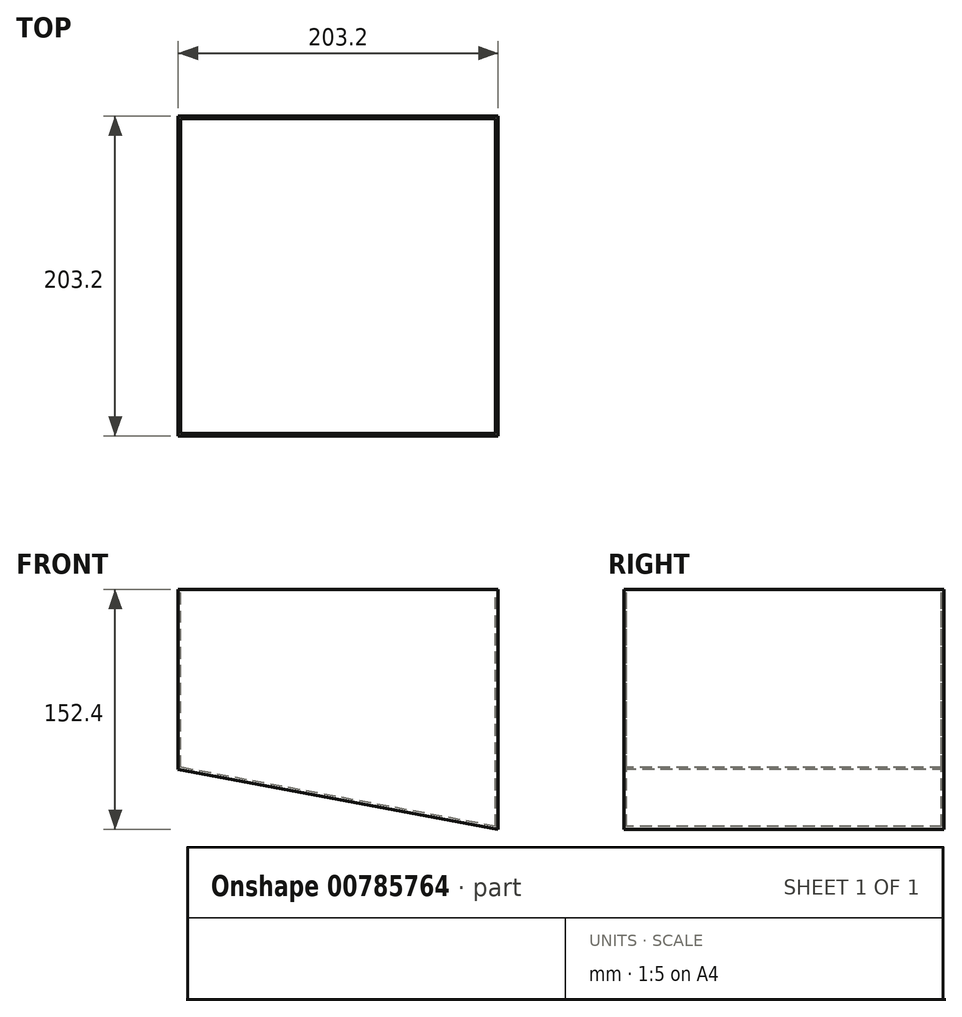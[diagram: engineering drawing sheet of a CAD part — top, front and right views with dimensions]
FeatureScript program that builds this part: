
annotation { "Feature Type Name" : "Feature", "Feature Type Description" : "" }
export const myFeature = defineFeature(function(context is Context, id is Id, definition is map)
    precondition{}
    {
        {
            var Q0;
            Q0=qCreatedBy(makeId("Front.planeOp"),FACE);
            var sketch = newSketch(context, id + "F0", { "sketchPlane" : qUnion([Q0])});
            skLineSegment(sketch, "E0.top", {"start": v(101.6, 76.2) * mm, "end": v(-101.6, 76.2) * mm});
            skLineSegment(sketch, "E0.left", {"start": v(101.6, -76.2) * mm, "end": v(101.6, 76.2) * mm});
            skLineSegment(sketch, "E0.right", {"start": v(-101.6, -38.1) * mm, "end": v(-101.6, 76.2) * mm});
            skPoint(sketch, "E0.middle", {"position": v(0, 0) * mm});
            skLineSegment(sketch, "E1", {"start": v(101.6, -76.2) * mm, "end": v(-101.6, -38.1) * mm});
            skPoint(sketch, "E0.bottom.end.orphan", {"position": v(-101.6, -76.2) * mm});
            skSolve(sketch);
        }
        {
            var Q0;
            Q0 = qSketchRegion(id + "F0", true);
            extrude(context, id + "F1", {"entities" : qUnion([Q0]), "oppositeDirection" : true, "depth" : 203.2 * mm, "offsetDistance" : 25.4 * mm});
        }
        {
            var Q0;
            Q0=makeQuery(id+"F1.opExtrude","SWEPT_FACE",FACE,{"disambiguationData":[OSD([sQuery(id+"F0.wireOp",EDGE,"E0.top")])]});
            shell(context, id + "F2", {"entities" : qUnion([Q0]), "thickness" : 1.57 * mm});
        }
    });
